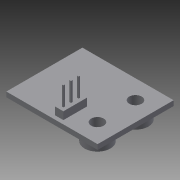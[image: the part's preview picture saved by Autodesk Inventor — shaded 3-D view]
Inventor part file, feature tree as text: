
AUTODESK INVENTOR PART (.ipt)
format: ipt  version: 2014 SP1 (Build 180222100, 222)  size: 123,904 bytes
history: native  units: in
note: dims shown in document units (in); Inventor stores cm internally (conversion verified against a paired STEP export)
features: extrude x1, other x1, imported_body x1
ambient origin geometry x8: Origin, YZ Plane, XZ Plane, XY Plane, X Axis, Y Axis, Z Axis, Center Point
bodies: Body1 (feature_tree)
feature tree (3):
  extrude  "Extrude6"  [1 undecoded]
  other  "276-2333-001 Rev21"
  imported_body  "Base1"
note: 1 required parameter value undecoded (feature->parameter linkage not recoverable at this tier; creation-order binding heuristic only, values carry confidence <= 0.55)
